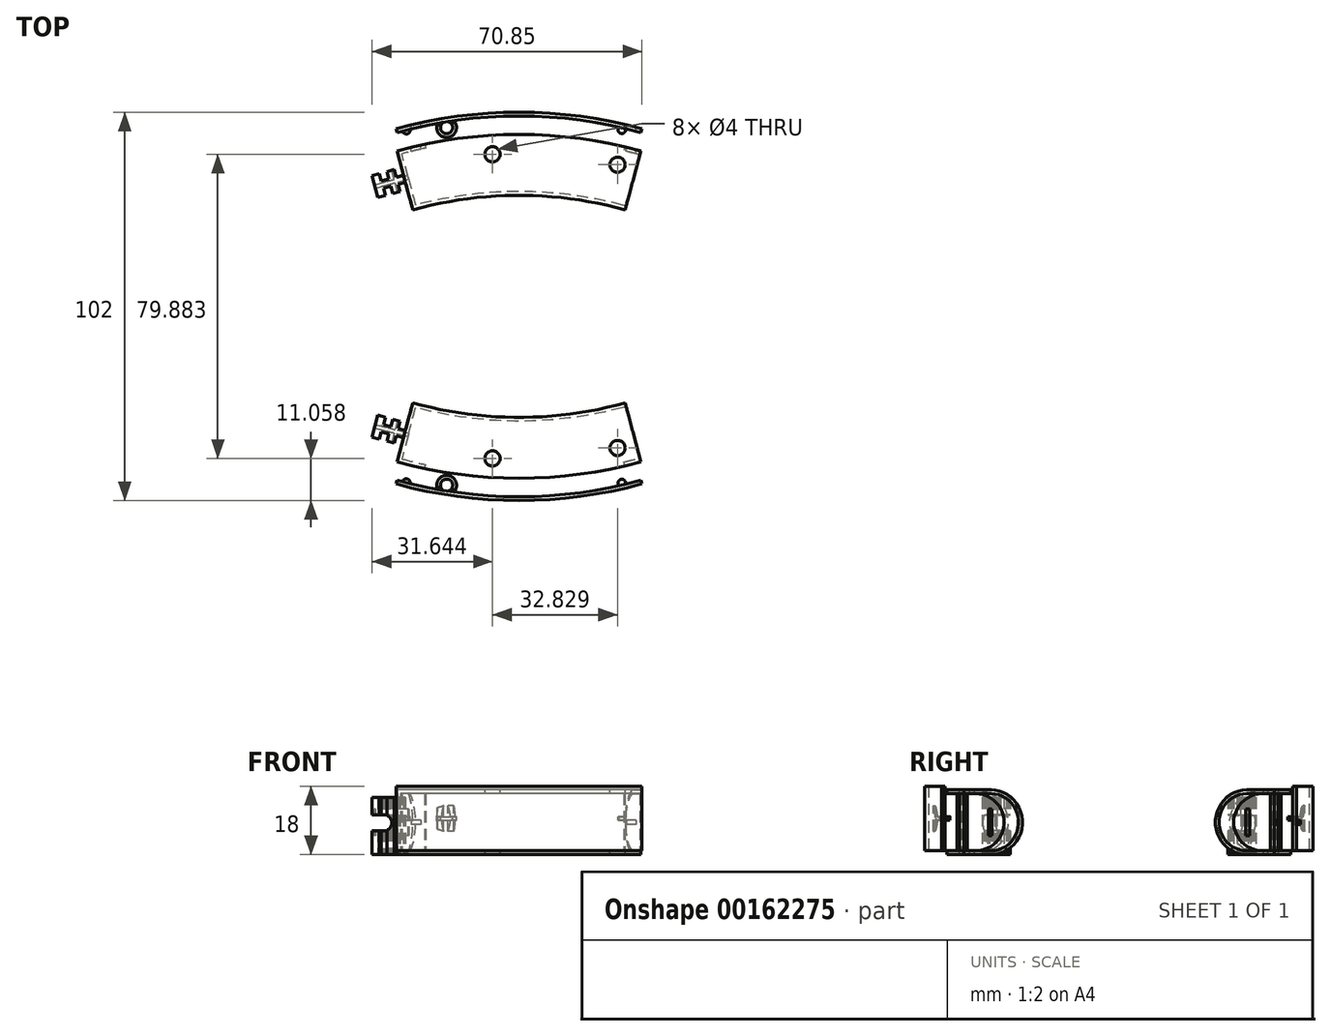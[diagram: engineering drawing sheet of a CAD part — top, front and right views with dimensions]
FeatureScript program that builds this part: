
annotation { "Feature Type Name" : "Feature", "Feature Type Description" : "" }
export const myFeature = defineFeature(function(context is Context, id is Id, definition is map)
    precondition{}
    {
        {
            var Q0;
            Q0=qCreatedBy(makeId("Front.planeOp"),FACE);
            cPlane(context, id + "F0", {"entities" : qUnion([Q0]), "cplaneType" : CPlaneType.OFFSET, "offset" : 50 * mm, "oppositeDirection" : true, "width" : 150 * mm, "height" : 150 * mm});
        }
        {
            var Q0;
            Q0=qCreatedBy(makeId("Top.planeOp"),FACE);
            var sketch = newSketch(context, id + "F1", { "sketchPlane" : qUnion([Q0])});
            skPoint(sketch, "E0.middle", {"position": v(-0.93, 0) * mm});
            skArc(sketch, "E1", {"start": v(-27.18, 26.57) * mm, "mid": v(0, 30.15) * mm, "end": v(27.18, 26.57) * mm});
            skArc(sketch, "E2", {"start": v(-31.06, 41.06) * mm, "mid": v(0, 45.15) * mm, "end": v(31.06, 41.06) * mm});
            skLineSegment(sketch, "E3", {"start": v(-27.18, 26.57) * mm, "end": v(-31.06, 41.06) * mm});
            skLineSegment(sketch, "E4", {"start": v(27.18, 26.57) * mm, "end": v(31.06, 41.06) * mm});
            skPoint(sketch, "E5.orphan", {"position": v(-73.64, 0) * mm});
            skPoint(sketch, "E6.orphan", {"position": v(73.64, 0) * mm});
            skPoint(sketch, "E0.left.start.orphan", {"position": v(24.07, 5) * mm});
            skPoint(sketch, "E0.top.start.orphan", {"position": v(24.07, -5) * mm});
            skPoint(sketch, "E0.right.end.orphan", {"position": v(-25.93, -5) * mm});
            skPoint(sketch, "E0.right.start.orphan", {"position": v(-25.93, 5) * mm});
            skSolve(sketch);
        }
        {
            var Q0;
            Q0 = qSketchRegion(id + "F1", true);
            extrude(context, id + "F2", {"entities" : qUnion([Q0]), "depth" : 15 * mm});
        }
        {
            var Q0;
            Q0=makeQuery(id+"F2.opExtrude","CAP_EDGE",EDGE,{"disambiguationData":[OSD([sQuery(id+"F1.wireOp",EDGE,"E1")])],"isStart":false});
            var Q1;
            Q1=makeQuery(id+"F2.opExtrude","CAP_EDGE",EDGE,{"disambiguationData":[OSD([sQuery(id+"F1.wireOp",EDGE,"E1")])],"isStart":true});
            fillet(context, id + "F3", {"entities" : qUnion([Q0, Q1]), "radius" : 7.5 * mm, "tangentPropagation" : true, "allowEdgeOverflow" : false});
        }
        {
            var Q0;
            Q0=makeQuery(id+"F2.opExtrude","SWEPT_FACE",FACE,{"disambiguationData":[OSD([sQuery(id+"F1.wireOp",EDGE,"E2")])]});
            shell(context, id + "F4", {"entities" : qUnion([Q0]), "thickness" : 1 * mm, "oppositeDirection" : true});
        }
        {
            var Q0;
            Q0=makeQuery(id+"F4.opShell","OFFSET_FACE",FACE,{"disambiguationData":[OSD([sQuery(id+"F1.wireOp",EDGE,"E4")])]});
            extrude(context, id + "F5", {"entities" : qUnion([Q0]), "operationType" : NewBodyOperationType.REMOVE, "oppositeDirection" : true, "depth" : 25 * mm});
        }
        {
            var Q0;
            Q0=makeQuery(id+"F2.opExtrude","CAP_FACE",FACE,{"disambiguationData":[OSD([sQuery(id+"F1.wireOp",EDGE,"E1"),sQuery(id+"F1.wireOp",EDGE,"E2"),sQuery(id+"F1.wireOp",EDGE,"E3"),sQuery(id+"F1.wireOp",EDGE,"E4")])],"isStart":false});
            var sketch = newSketch(context, id + "F6", { "sketchPlane" : qUnion([Q0])});
            skCircle(sketch, "E7", {"center": v(25.88, 37.2) * mm, "radius": 2 * mm});
            skCircle(sketch, "E8", {"center": v(-6.95, 39.94) * mm, "radius": 2 * mm});
            skSolve(sketch);
        }
        {
            var Q0;
            Q0 = qSketchRegion(id + "F6", true);
            extrude(context, id + "F7", {"entities" : qUnion([Q0]), "operationType" : NewBodyOperationType.REMOVE, "endBound" : BoundingType.THROUGH_ALL, "oppositeDirection" : true, "depth" : 25 * mm});
        }
        {
            var Q0;
            Q0=makeQuery(id+"F2.opExtrude","SWEPT_FACE",FACE,{"disambiguationData":[OSD([sQuery(id+"F1.wireOp",EDGE,"E3")])]});
            var sketch = newSketch(context, id + "F8", { "sketchPlane" : qUnion([Q0])});
            skLineSegment(sketch, "E9.bottom", {"start": v(-39.7, 11) * mm, "end": v(-40.7, 11) * mm});
            skLineSegment(sketch, "E9.top", {"start": v(-39.7, 4) * mm, "end": v(-40.7, 4) * mm});
            skLineSegment(sketch, "E9.left", {"start": v(-39.7, 11) * mm, "end": v(-39.7, 4) * mm});
            skLineSegment(sketch, "E9.right", {"start": v(-40.7, 11) * mm, "end": v(-40.7, 4) * mm});
            skPoint(sketch, "E9.middle", {"position": v(-40.2, 7.5) * mm});
            skPoint(sketch, "E9.middle.positionSnap0", {"position": v(-47.7, 7.5) * mm});
            skPoint(sketch, "E9.centerSnap0", {"position": v(-47.7, 7.5) * mm});
            skSolve(sketch);
        }
        {
            var Q0;
            Q0=makeQuery(id+"F2.opExtrude","CAP_FACE",FACE,{"disambiguationData":[OSD([sQuery(id+"F1.wireOp",EDGE,"E1"),sQuery(id+"F1.wireOp",EDGE,"E2"),sQuery(id+"F1.wireOp",EDGE,"E3"),sQuery(id+"F1.wireOp",EDGE,"E4")])],"isStart":true});
            var sketch = newSketch(context, id + "F9", { "sketchPlane" : qUnion([Q0])});
            skLineSegment(sketch, "E10", {"start": v(-30.08, -33.56) * mm, "end": v(-39.65, -31) * mm, "construction": true});
            skLineSegment(sketch, "E11", {"start": v(-29.82, -32.59) * mm, "end": v(-31.75, -32.07) * mm});
            skLineSegment(sketch, "E12", {"start": v(-31.75, -32.07) * mm, "end": v(-31.24, -30.14) * mm});
            skLineSegment(sketch, "E13", {"start": v(-31.24, -30.14) * mm, "end": v(-33.17, -29.62) * mm});
            skLineSegment(sketch, "E14", {"start": v(-33.17, -29.62) * mm, "end": v(-33.69, -31.55) * mm});
            skLineSegment(sketch, "E15", {"start": v(-33.69, -31.55) * mm, "end": v(-35.62, -31.04) * mm});
            skLineSegment(sketch, "E16", {"start": v(-35.62, -31.04) * mm, "end": v(-35.1, -29.1) * mm});
            skLineSegment(sketch, "E17", {"start": v(-35.1, -29.1) * mm, "end": v(-37.03, -28.59) * mm});
            skLineSegment(sketch, "E18", {"start": v(-37.03, -28.59) * mm, "end": v(-38.59, -34.38) * mm});
            skLineSegment(sketch, "E19", {"start": v(-38.59, -34.38) * mm, "end": v(-36.65, -34.9) * mm});
            skLineSegment(sketch, "E20", {"start": v(-36.65, -34.9) * mm, "end": v(-36.14, -32.97) * mm});
            skLineSegment(sketch, "E21", {"start": v(-36.14, -32.97) * mm, "end": v(-34.2, -33.49) * mm});
            skLineSegment(sketch, "E22", {"start": v(-34.2, -33.49) * mm, "end": v(-34.72, -35.42) * mm});
            skLineSegment(sketch, "E23", {"start": v(-34.72, -35.42) * mm, "end": v(-32.8, -35.94) * mm});
            skLineSegment(sketch, "E24", {"start": v(-32.8, -35.94) * mm, "end": v(-32.27, -34) * mm});
            skLineSegment(sketch, "E25", {"start": v(-32.27, -34) * mm, "end": v(-30.34, -34.52) * mm});
            skLineSegment(sketch, "E26", {"start": v(-30.34, -34.52) * mm, "end": v(-29.82, -32.59) * mm});
            skSolve(sketch);
        }
        {
            var Q0;
            Q0 = qSketchRegion(id + "F9", true);
            extrude(context, id + "F10", {"entities" : qUnion([Q0]), "operationType" : NewBodyOperationType.ADD, "oppositeDirection" : true, "depth" : 15 * mm});
        }
        {
            var Q0;
            Q0 = qSketchRegion(id + "F8", true);
            extrude(context, id + "F11", {"entities" : qUnion([Q0]), "operationType" : NewBodyOperationType.REMOVE, "oppositeDirection" : true, "depth" : 5 * mm, "hasSecondDirection" : true, "secondDirectionOppositeDirection" : false, "secondDirectionDepth" : 25 * mm});
        }
        {
            var Q0;
            Q0=makeQuery(id+"F10.opExtrude","SWEPT_FACE",FACE,{"disambiguationData":[OSD([sQuery(id+"F9.wireOp",EDGE,"E18")])]});
            var sketch = newSketch(context, id + "F12", { "sketchPlane" : qUnion([Q0])});
            skLineSegment(sketch, "E27.bottom", {"start": v(-36.4, 5.3) * mm, "end": v(-44.55, 5.3) * mm});
            skLineSegment(sketch, "E27.top", {"start": v(-36.4, 9.4) * mm, "end": v(-44.55, 9.4) * mm});
            skLineSegment(sketch, "E27.left", {"start": v(-36.4, 5.3) * mm, "end": v(-36.4, 9.4) * mm});
            skLineSegment(sketch, "E27.right", {"start": v(-44.55, 5.3) * mm, "end": v(-44.55, 9.4) * mm});
            skSolve(sketch);
        }
        {
            var Q0;
            Q0 = qSketchRegion(id + "F12", true);
            extrude(context, id + "F13", {"entities" : qUnion([Q0]), "operationType" : NewBodyOperationType.REMOVE, "oppositeDirection" : true, "depth" : 5.35 * mm});
        }
        {
            var Q0;
            {var subQ0=sQuery(id+"F12.wireOp",EDGE,"E27.top");Q0=makeQuery(id+"F13.boolean.opBoolean","COPY",EDGE,{"disambiguationData":[TD([makeQuery(id+"F10.opExtrude","SWEPT_FACE",FACE,{"disambiguationData":[OSD([sQuery(id+"F9.wireOp",EDGE,"E13")])]})])],"derivedFrom":makeQuery(id+"F13.opExtrude","CAP_EDGE",EDGE,{"disambiguationData":[OSD([subQ0])],"isStart":false})});}
            var Q1;
            {var subQ0=sQuery(id+"F12.wireOp",EDGE,"E27.top");Q1=makeQuery(id+"F13.boolean.opBoolean","COPY",EDGE,{"disambiguationData":[TD([makeQuery(id+"F10.opExtrude","SWEPT_FACE",FACE,{"disambiguationData":[OSD([sQuery(id+"F9.wireOp",EDGE,"E23")])]})])],"derivedFrom":makeQuery(id+"F13.opExtrude","CAP_EDGE",EDGE,{"disambiguationData":[OSD([subQ0])],"isStart":false})});}
            var Q2;
            {var subQ0=sQuery(id+"F12.wireOp",EDGE,"E27.bottom");Q2=makeQuery(id+"F13.boolean.opBoolean","COPY",EDGE,{"disambiguationData":[TD([makeQuery(id+"F10.opExtrude","SWEPT_FACE",FACE,{"disambiguationData":[OSD([sQuery(id+"F9.wireOp",EDGE,"E13")])]})])],"derivedFrom":makeQuery(id+"F13.opExtrude","CAP_EDGE",EDGE,{"disambiguationData":[OSD([subQ0])],"isStart":false})});}
            var Q3;
            {var subQ0=sQuery(id+"F12.wireOp",EDGE,"E27.bottom");Q3=makeQuery(id+"F13.boolean.opBoolean","COPY",EDGE,{"disambiguationData":[TD([makeQuery(id+"F10.opExtrude","SWEPT_FACE",FACE,{"disambiguationData":[OSD([sQuery(id+"F9.wireOp",EDGE,"E23")])]})])],"derivedFrom":makeQuery(id+"F13.opExtrude","CAP_EDGE",EDGE,{"disambiguationData":[OSD([subQ0])],"isStart":false})});}
            fillet(context, id + "F14", {"entities" : qUnion([Q0, Q1, Q2, Q3]), "radius" : 2 * mm, "tangentPropagation" : true, "allowEdgeOverflow" : false});
        }
        {
            var Q0;
            Q0=qCreatedBy(makeId("Top.planeOp"),FACE);
            var sketch = newSketch(context, id + "F15", { "sketchPlane" : qUnion([Q0])});
            skArc(sketch, "E28", {"start": v(32, 40.77) * mm, "mid": v(29.9, 41.33) * mm, "end": v(27.78, 41.86) * mm});
            skArc(sketch, "E29", {"start": v(31.76, 39.8) * mm, "mid": v(29.64, 40.36) * mm, "end": v(27.52, 40.89) * mm});
            skLineSegment(sketch, "E30", {"start": v(31.76, 39.8) * mm, "end": v(32, 40.77) * mm});
            skLineSegment(sketch, "E31", {"start": v(-32.02, 40.76) * mm, "end": v(-31.74, 39.8) * mm});
            skLineSegment(sketch, "E32", {"start": v(27.78, 41.86) * mm, "end": v(27.52, 40.89) * mm});
            skLineSegment(sketch, "E33", {"start": v(-24.82, 42.52) * mm, "end": v(-24.54, 41.56) * mm});
            skArc(sketch, "E34.trimOffspring", {"start": v(-24.82, 42.52) * mm, "mid": v(-28.44, 41.7) * mm, "end": v(-32.02, 40.76) * mm});
            skArc(sketch, "E35.trimOffspring", {"start": v(-24.54, 41.56) * mm, "mid": v(-28.16, 40.74) * mm, "end": v(-31.74, 39.8) * mm});
            skSolve(sketch);
        }
        {
            var Q0;
            Q0 = qSketchRegion(id + "F15", true);
            extrude(context, id + "F16", {"entities" : qUnion([Q0]), "operationType" : NewBodyOperationType.ADD, "depth" : 15 * mm});
        }
        {
            var Q0;
            Q0=qCreatedBy(makeId("Top.planeOp"),FACE);
            var sketch = newSketch(context, id + "F17", { "sketchPlane" : qUnion([Q0])});
            skArc(sketch, "E36", {"start": v(-32, 45.65) * mm, "mid": v(0, 50) * mm, "end": v(32, 45.66) * mm});
            skArc(sketch, "E37", {"start": v(-32.27, 46.62) * mm, "mid": v(0, 51) * mm, "end": v(32.26, 46.62) * mm});
            skLineSegment(sketch, "E38", {"start": v(-32.27, 46.62) * mm, "end": v(-32, 45.65) * mm});
            skLineSegment(sketch, "E39", {"start": v(32, 45.66) * mm, "end": v(32.26, 46.62) * mm});
            skSolve(sketch);
        }
        {
            var Q0;
            Q0 = qSketchRegion(id + "F17", true);
            extrude(context, id + "F18", {"entities" : qUnion([Q0]), "depth" : 17 * mm});
        }
        {
            var Q0;
            Q0=qCreatedBy(makeId("Top.planeOp"),FACE);
            cPlane(context, id + "F19", {"entities" : qUnion([Q0]), "cplaneType" : CPlaneType.OFFSET, "offset" : 8.5 * mm, "width" : 150 * mm, "height" : 150 * mm});
        }
        {
            var Q0;
            Q0=qCreatedBy(id+"F19.planeOp",FACE);
            var sketch = newSketch(context, id + "F20", { "sketchPlane" : qUnion([Q0])});
            skArc(sketch, "E40", {"start": v(-21.39, 48) * mm, "mid": v(-18.43, 44.44) * mm, "end": v(-17.32, 48.94) * mm});
            skArc(sketch, "E41", {"start": v(-19.77, 48.37) * mm, "mid": v(-18.59, 45.43) * mm, "end": v(-19.06, 48.56) * mm});
            skLineSegment(sketch, "E42", {"start": v(-21.39, 48) * mm, "end": v(-19.77, 48.37) * mm});
            skLineSegment(sketch, "E43", {"start": v(-19.06, 48.56) * mm, "end": v(-17.32, 48.94) * mm});
            skCircle(sketch, "E44", {"center": v(-29.6, 46.3) * mm, "radius": 1 * mm});
            skCircle(sketch, "E45", {"center": v(27.01, 46.4) * mm, "radius": 1 * mm});
            skSolve(sketch);
        }
        {
            var Q0;
            Q0 = qSketchRegion(id + "F20", true);
            extrude(context, id + "F21", {"entities" : qUnion([Q0]), "operationType" : NewBodyOperationType.ADD, "endBound" : BoundingType.SYMMETRIC, "oppositeDirection" : true, "depth" : 1 * mm});
        }
        {
            var Q0;
            Q0=makeQuery(id+"F21.boolean.opBoolean","INTERSECT",EDGE,{"disambiguationData":[OD(0.0)],"derivedFrom":[makeQuery(id+"F18.opExtrude","SWEPT_FACE",FACE,{"disambiguationData":[OSD([sQuery(id+"F17.wireOp",EDGE,"E36")])]}),makeQuery(id+"F21.opExtrude","CAP_FACE",FACE,{"disambiguationData":[OSD([sQuery(id+"F20.wireOp",EDGE,"E40"),sQuery(id+"F20.wireOp",EDGE,"E41"),sQuery(id+"F20.wireOp",EDGE,"E42"),sQuery(id+"F20.wireOp",EDGE,"E43")])],"isStart":false})]});
            var Q1;
            Q1=makeQuery(id+"F21.boolean.opBoolean","INTERSECT",EDGE,{"disambiguationData":[OD(1.0)],"derivedFrom":[makeQuery(id+"F18.opExtrude","SWEPT_FACE",FACE,{"disambiguationData":[OSD([sQuery(id+"F17.wireOp",EDGE,"E36")])]}),makeQuery(id+"F21.opExtrude","CAP_FACE",FACE,{"disambiguationData":[OSD([sQuery(id+"F20.wireOp",EDGE,"E40"),sQuery(id+"F20.wireOp",EDGE,"E41"),sQuery(id+"F20.wireOp",EDGE,"E42"),sQuery(id+"F20.wireOp",EDGE,"E43")])],"isStart":false})]});
            var Q2;
            Q2=makeQuery(id+"F21.boolean.opBoolean","INTERSECT",EDGE,{"disambiguationData":[OD(0.0)],"derivedFrom":[makeQuery(id+"F18.opExtrude","SWEPT_FACE",FACE,{"disambiguationData":[OSD([sQuery(id+"F17.wireOp",EDGE,"E36")])]}),makeQuery(id+"F21.opExtrude","CAP_FACE",FACE,{"disambiguationData":[OSD([sQuery(id+"F20.wireOp",EDGE,"E40"),sQuery(id+"F20.wireOp",EDGE,"E41"),sQuery(id+"F20.wireOp",EDGE,"E42"),sQuery(id+"F20.wireOp",EDGE,"E43")])],"isStart":true})]});
            var Q3;
            Q3=makeQuery(id+"F21.boolean.opBoolean","INTERSECT",EDGE,{"disambiguationData":[OD(1.0)],"derivedFrom":[makeQuery(id+"F18.opExtrude","SWEPT_FACE",FACE,{"disambiguationData":[OSD([sQuery(id+"F17.wireOp",EDGE,"E36")])]}),makeQuery(id+"F21.opExtrude","CAP_FACE",FACE,{"disambiguationData":[OSD([sQuery(id+"F20.wireOp",EDGE,"E40"),sQuery(id+"F20.wireOp",EDGE,"E41"),sQuery(id+"F20.wireOp",EDGE,"E42"),sQuery(id+"F20.wireOp",EDGE,"E43")])],"isStart":true})]});
            chamfer(context, id + "F22", {"entities" : qUnion([Q0, Q1, Q2, Q3]), "chamferType" : ChamferType.OFFSET_ANGLE, "width" : 0.5 * mm, "oppositeDirection" : true, "angle" : 80 * degree, "tangentPropagation" : true});
        }
        {
            var Q0;
            Q0=makeQuery(id+"F2.opExtrude","SWEPT_BODY",BODY,{"disambiguationData":[OSD([sQuery(id+"F1.wireOp",EDGE,"E1"),sQuery(id+"F1.wireOp",EDGE,"E2"),sQuery(id+"F1.wireOp",EDGE,"E3"),sQuery(id+"F1.wireOp",EDGE,"E4")])]});
            var Q1;
            Q1=makeQuery(id+"F18.opExtrude","SWEPT_BODY",BODY,{"disambiguationData":[OSD([sQuery(id+"F17.wireOp",EDGE,"E36"),sQuery(id+"F17.wireOp",EDGE,"E37"),sQuery(id+"F17.wireOp",EDGE,"E38"),sQuery(id+"F17.wireOp",EDGE,"E39")])]});
            var Q2;
            Q2=qCreatedBy(makeId("Front.planeOp"),FACE);
            mirror(context, id + "F23", {"entities" : qUnion([Q0, Q1]), "mirrorPlane" : qUnion([Q2])});
        }
        {
            var Q0;
            Q0=qCreatedBy(id+"F0.planeOp",FACE);
            var sketch = newSketch(context, id + "F24", { "sketchPlane" : qUnion([Q0])});
            skLineSegment(sketch, "E46", {"start": v(44.5, 7.5) * mm, "end": v(-49.91, 7.5) * mm, "construction": true});
            skLineSegment(sketch, "E47.bottom", {"start": v(28.2, 8.1) * mm, "end": v(30.7, 8.1) * mm});
            skLineSegment(sketch, "E47.top", {"start": v(28.2, 6.9) * mm, "end": v(30.7, 6.9) * mm});
            skLineSegment(sketch, "E47.left", {"start": v(28.2, 8.1) * mm, "end": v(28.2, 6.9) * mm});
            skLineSegment(sketch, "E47.right", {"start": v(30.7, 8.1) * mm, "end": v(30.7, 6.9) * mm});
            skPoint(sketch, "E47.middle", {"position": v(29.45, 7.5) * mm});
            skLineSegment(sketch, "E48.bottom", {"start": v(-28.27, 8.1) * mm, "end": v(-25.77, 8.1) * mm});
            skLineSegment(sketch, "E48.top", {"start": v(-28.27, 6.9) * mm, "end": v(-25.77, 6.9) * mm});
            skLineSegment(sketch, "E48.left", {"start": v(-28.27, 8.1) * mm, "end": v(-28.27, 6.9) * mm});
            skLineSegment(sketch, "E48.right", {"start": v(-25.77, 8.1) * mm, "end": v(-25.77, 6.9) * mm});
            skPoint(sketch, "E48.middle", {"position": v(-27.02, 7.5) * mm});
            skSolve(sketch);
        }
        {
            var Q0;
            Q0 = qSketchRegion(id + "F24", true);
            extrude(context, id + "F25", {"entities" : qUnion([Q0]), "operationType" : NewBodyOperationType.REMOVE, "depth" : 12.75 * mm});
        }
    });
